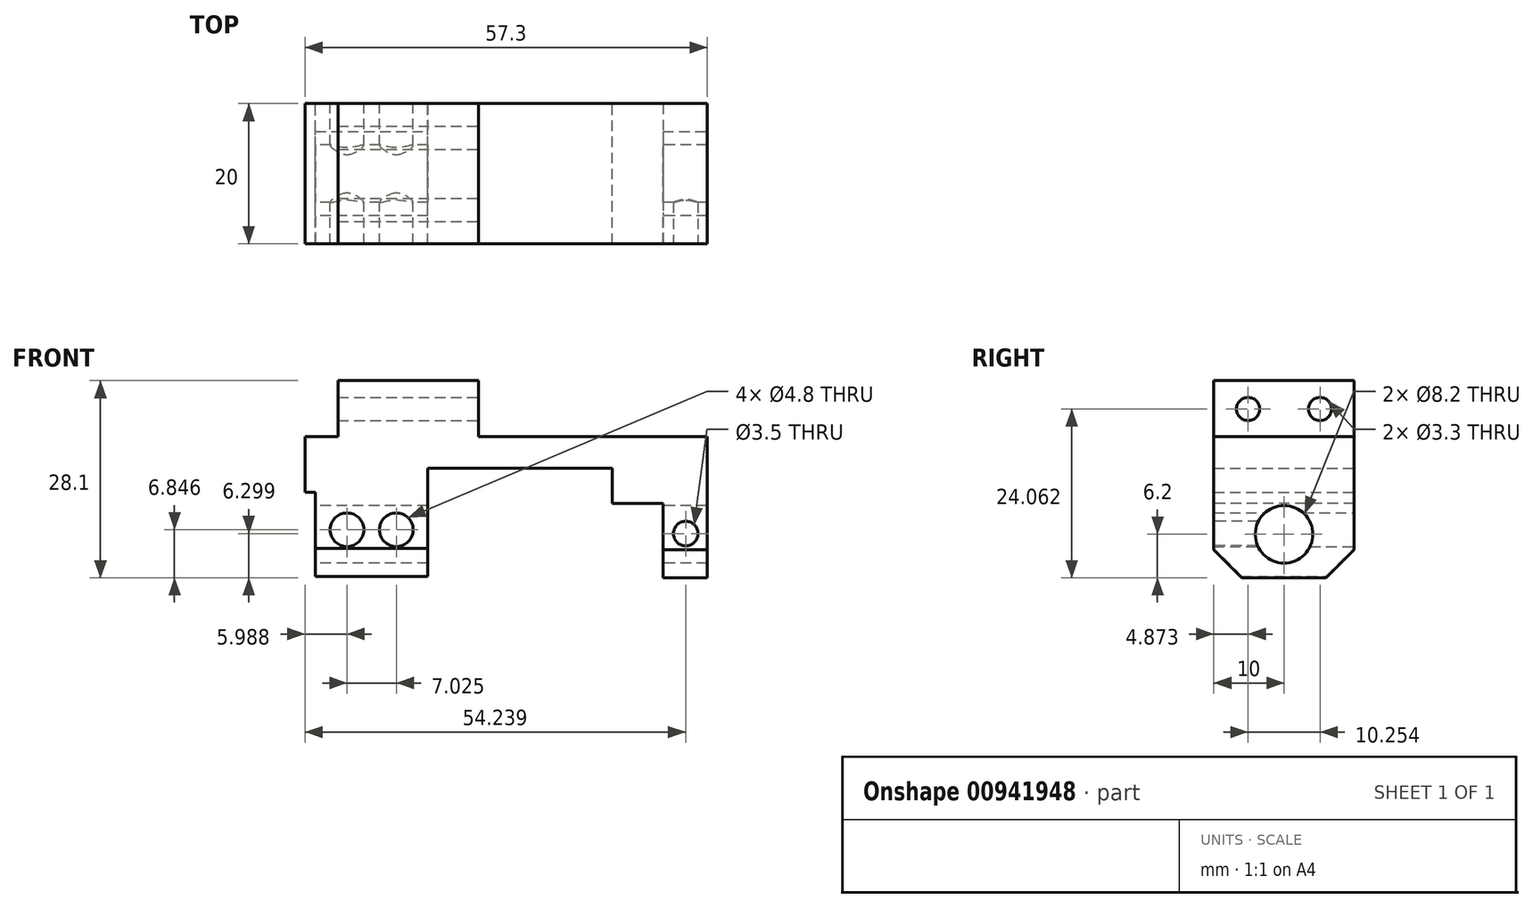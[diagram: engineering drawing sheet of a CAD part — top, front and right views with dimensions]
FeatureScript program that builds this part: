
annotation { "Feature Type Name" : "Feature", "Feature Type Description" : "" }
export const myFeature = defineFeature(function(context is Context, id is Id, definition is map)
    precondition{}
    {
        {
            var Q0;
            Q0=qCreatedBy(makeId("Front.planeOp"),FACE);
            var sketch = newSketch(context, id + "F0", { "sketchPlane" : qUnion([Q0])});
            skPoint(sketch, "E0.middle", {"position": v(0, 0) * mm});
            skLineSegment(sketch, "E1", {"start": v(-27, 4.5) * mm, "end": v(-22.3, 4.5) * mm});
            skLineSegment(sketch, "E2", {"start": v(-22.3, 4.5) * mm, "end": v(-22.3, 12.5) * mm});
            skPoint(sketch, "E3.orphan", {"position": v(-24.1, 12.5) * mm});
            skLineSegment(sketch, "E4", {"start": v(-2.3, 12.5) * mm, "end": v(-2.3, 4.5) * mm});
            skLineSegment(sketch, "E5", {"start": v(-2.3, 4.5) * mm, "end": v(27, 4.5) * mm});
            skPoint(sketch, "E6.orphan", {"position": v(27, 14) * mm});
            skLineSegment(sketch, "E7", {"start": v(-22.3, 12.5) * mm, "end": v(-2.3, 12.5) * mm});
            skLineSegment(sketch, "E8", {"start": v(-27, 4.5) * mm, "end": v(-27, -3.4) * mm});
            skLineSegment(sketch, "E9", {"start": v(-27, -3.4) * mm, "end": v(-25.5, -3.4) * mm});
            skLineSegment(sketch, "E10", {"start": v(-25.5, -3.4) * mm, "end": v(-25.5, -15.4) * mm});
            skPoint(sketch, "E11.orphan", {"position": v(-27, -14) * mm});
            skLineSegment(sketch, "E12", {"start": v(-25.5, -15.4) * mm, "end": v(-9.5, -15.4) * mm});
            skPoint(sketch, "E0.right.end.orphan", {"position": v(24.1, -12.5) * mm});
            skLineSegment(sketch, "E13", {"start": v(27, 4.5) * mm, "end": v(27, 0) * mm});
            skLineSegment(sketch, "E14", {"start": v(-9.5, -15.4) * mm, "end": v(-9.5, 0) * mm});
            skLineSegment(sketch, "E15", {"start": v(-9.5, 0) * mm, "end": v(16.8, 0) * mm});
            skLineSegment(sketch, "E16", {"start": v(27, 0) * mm, "end": v(27, -5) * mm});
            skLineSegment(sketch, "E17", {"start": v(27, -5) * mm, "end": v(16.8, -5) * mm});
            skLineSegment(sketch, "E18", {"start": v(16.8, -5) * mm, "end": v(16.8, 0) * mm});
            skSolve(sketch);
        }
        {
            var Q0;
            Q0 = qSketchRegion(id + "F0", true);
            extrude(context, id + "F1", {"entities" : qUnion([Q0]), "endBound" : BoundingType.SYMMETRIC, "depth" : 20 * mm, "offsetDistance" : 25 * mm});
        }
        {
            var Q0;
            Q0=makeQuery(id+"F1.opExtrude","CAP_EDGE",EDGE,{"disambiguationData":[OSD([sQuery(id+"F0.wireOp",EDGE,"E12")])],"isStart":false});
            var Q1;
            Q1=makeQuery(id+"F1.opExtrude","CAP_EDGE",EDGE,{"disambiguationData":[OSD([sQuery(id+"F0.wireOp",EDGE,"E12")])],"isStart":true});
            chamfer(context, id + "F2", {"entities" : qUnion([Q0, Q1]), "width" : 4 * mm, "tangentPropagation" : true});
        }
        {
            var Q0;
            Q0=makeQuery(id+"F1.opExtrude","SWEPT_FACE",FACE,{"disambiguationData":[OSD([sQuery(id+"F0.wireOp",EDGE,"E10")])]});
            var sketch = newSketch(context, id + "F3", { "sketchPlane" : qUnion([Q0])});
            skLineSegment(sketch, "E19", {"start": v(0, -3.4) * mm, "end": v(0, -15.4) * mm});
            skCircle(sketch, "E20", {"center": v(0, -9.4) * mm, "radius": 4.1 * mm});
            skSolve(sketch);
        }
        {
            var Q0;
            Q0=makeQuery(id+"F1.opExtrude","SWEPT_FACE",FACE,{"disambiguationData":[OSD([sQuery(id+"F0.wireOp",EDGE,"E13"),sQuery(id+"F0.wireOp",EDGE,"E16")])]});
            var sketch = newSketch(context, id + "F4", { "sketchPlane" : qUnion([Q0])});
            skLineSegment(sketch, "E21", {"start": v(10, 4.5) * mm, "end": v(10, -15.6) * mm});
            skLineSegment(sketch, "E22", {"start": v(10, -15.6) * mm, "end": v(-10, -15.6) * mm});
            skPoint(sketch, "E23.end.orphan", {"position": v(-10, -14.05) * mm});
            skLineSegment(sketch, "E24", {"start": v(-10, -15.6) * mm, "end": v(-10, 4.5) * mm});
            skLineSegment(sketch, "E25", {"start": v(-10, 4.5) * mm, "end": v(10, 4.5) * mm});
            skSolve(sketch);
        }
        {
            var Q0;
            Q0 = qSketchRegion(id + "F4", true);
            extrude(context, id + "F5", {"entities" : qUnion([Q0]), "operationType" : NewBodyOperationType.ADD, "depth" : 3.3 * mm, "offsetDistance" : 25 * mm, "hasSecondDirection" : true, "secondDirectionOppositeDirection" : true, "secondDirectionDepth" : 3 * mm});
        }
        {
            var Q0;
            {var subQ0=sQuery(id+"F3.wireOp",EDGE,"E20");var subQ1=sQuery(id+"F3.wireOp",EDGE,"E19");var subQ2=makeQuery(id+"F3.imprint","INTERSECT",VERTEX,{"disambiguationData":[OD(0.0)],"derivedFrom":[subQ1,subQ0]});Q0=makeQuery(id+"F3.imprint","IMPRINT",FACE,{"disambiguationData":[TD([[makeQuery(id+"F3.imprint","IMPRINT",EDGE,{"disambiguationData":[TD([[subQ2,-1.0]])],"derivedFrom":subQ1}),1.0]])]});}
            var Q1;
            {var subQ0=sQuery(id+"F3.wireOp",EDGE,"E20");var subQ1=sQuery(id+"F3.wireOp",EDGE,"E19");var subQ2=makeQuery(id+"F3.imprint","INTERSECT",VERTEX,{"disambiguationData":[OD(0.0)],"derivedFrom":[subQ1,subQ0]});Q1=makeQuery(id+"F3.imprint","IMPRINT",FACE,{"disambiguationData":[TD([[makeQuery(id+"F3.imprint","IMPRINT",EDGE,{"disambiguationData":[TD([[subQ2,-1.0]])],"derivedFrom":subQ1}),-1.0]])]});}
            extrude(context, id + "F6", {"entities" : qUnion([Q0, Q1]), "operationType" : NewBodyOperationType.REMOVE, "oppositeDirection" : true, "depth" : 84 * mm, "offsetDistance" : 25 * mm});
        }
        {
            var Q0;
            Q0=makeQuery(id+"F5.opExtrude","SWEPT_EDGE",EDGE,{"disambiguationData":[OSD([sQuery(id+"F4.wireOp",EDGE,"E21"),sQuery(id+"F4.wireOp",EDGE,"E22")])]});
            var Q1;
            Q1=makeQuery(id+"F5.opExtrude","SWEPT_EDGE",EDGE,{"disambiguationData":[OSD([sQuery(id+"F4.wireOp",EDGE,"E22"),sQuery(id+"F4.wireOp",EDGE,"E24")])]});
            chamfer(context, id + "F7", {"entities" : qUnion([Q0, Q1]), "width" : 4 * mm, "tangentPropagation" : true});
        }
        {
            var Q0;
            Q0=makeQuery(id+"F5.boolean.opBoolean","MERGE",FACE,{"derivedFrom":[makeQuery(id+"F1.opExtrude","CAP_FACE",FACE,{"disambiguationData":[OSD([sQuery(id+"F0.wireOp",EDGE,"E1"),sQuery(id+"F0.wireOp",EDGE,"E2"),sQuery(id+"F0.wireOp",EDGE,"E4"),sQuery(id+"F0.wireOp",EDGE,"E5"),sQuery(id+"F0.wireOp",EDGE,"E7"),sQuery(id+"F0.wireOp",EDGE,"E8"),sQuery(id+"F0.wireOp",EDGE,"E9"),sQuery(id+"F0.wireOp",EDGE,"E10"),sQuery(id+"F0.wireOp",EDGE,"E12"),sQuery(id+"F0.wireOp",EDGE,"E13"),sQuery(id+"F0.wireOp",EDGE,"E14"),sQuery(id+"F0.wireOp",EDGE,"E15"),sQuery(id+"F0.wireOp",EDGE,"E16"),sQuery(id+"F0.wireOp",EDGE,"E17"),sQuery(id+"F0.wireOp",EDGE,"E18")])],"isStart":false}),makeQuery(id+"F5.opExtrude","SWEPT_FACE",FACE,{"disambiguationData":[OSD([sQuery(id+"F4.wireOp",EDGE,"E24")])]})]});
            var sketch = newSketch(context, id + "F8", { "sketchPlane" : qUnion([Q0])});
            skCircle(sketch, "E26", {"center": v(27.24, -9.3) * mm, "radius": 1.75 * mm});
            skSolve(sketch);
        }
        {
            var Q0;
            Q0 = qSketchRegion(id + "F8", true);
            extrude(context, id + "F9", {"entities" : qUnion([Q0]), "operationType" : NewBodyOperationType.REMOVE, "oppositeDirection" : true, "depth" : 8.7 * mm, "offsetDistance" : 25 * mm});
        }
        {
            var Q0;
            Q0=makeQuery(id+"F5.opExtrude","CAP_FACE",FACE,{"disambiguationData":[OSD([sQuery(id+"F4.wireOp",EDGE,"E21"),sQuery(id+"F4.wireOp",EDGE,"E22"),sQuery(id+"F4.wireOp",EDGE,"E24"),sQuery(id+"F4.wireOp",EDGE,"E25")])],"isStart":false});
            var sketch = newSketch(context, id + "F10", { "sketchPlane" : qUnion([Q0])});
            skLineSegment(sketch, "E27", {"start": v(10, 4.5) * mm, "end": v(10, 12.42) * mm});
            skLineSegment(sketch, "E28", {"start": v(10, 8.46) * mm, "end": v(6.75, 8.46) * mm});
            skCircle(sketch, "E29", {"center": v(5.13, 8.46) * mm, "radius": 1.65 * mm});
            skLineSegment(sketch, "E30", {"start": v(0, 0) * mm, "end": v(0, 3.04) * mm});
            skCircle(sketch, "E31.MirrorC", {"center": v(-5.13, 8.46) * mm, "radius": 1.65 * mm});
            skSolve(sketch);
        }
        {
            var Q0;
            Q0 = qSketchRegion(id + "F10", true);
            extrude(context, id + "F11", {"entities" : qUnion([Q0]), "operationType" : NewBodyOperationType.REMOVE, "oppositeDirection" : true, "depth" : 66.9 * mm, "offsetDistance" : 25 * mm});
        }
        {
            var Q0;
            Q0=makeQuery(id+"F5.boolean.opBoolean","MERGE",FACE,{"derivedFrom":[makeQuery(id+"F1.opExtrude","CAP_FACE",FACE,{"disambiguationData":[OSD([sQuery(id+"F0.wireOp",EDGE,"E1"),sQuery(id+"F0.wireOp",EDGE,"E2"),sQuery(id+"F0.wireOp",EDGE,"E4"),sQuery(id+"F0.wireOp",EDGE,"E5"),sQuery(id+"F0.wireOp",EDGE,"E7"),sQuery(id+"F0.wireOp",EDGE,"E8"),sQuery(id+"F0.wireOp",EDGE,"E9"),sQuery(id+"F0.wireOp",EDGE,"E10"),sQuery(id+"F0.wireOp",EDGE,"E12"),sQuery(id+"F0.wireOp",EDGE,"E13"),sQuery(id+"F0.wireOp",EDGE,"E14"),sQuery(id+"F0.wireOp",EDGE,"E15"),sQuery(id+"F0.wireOp",EDGE,"E16"),sQuery(id+"F0.wireOp",EDGE,"E17"),sQuery(id+"F0.wireOp",EDGE,"E18")])],"isStart":true}),makeQuery(id+"F5.opExtrude","SWEPT_FACE",FACE,{"disambiguationData":[OSD([sQuery(id+"F4.wireOp",EDGE,"E21")])]})]});
            var sketch = newSketch(context, id + "F12", { "sketchPlane" : qUnion([Q0])});
            skCircle(sketch, "E32", {"center": v(21.01, -8.75) * mm, "radius": 2.4 * mm});
            skLineSegment(sketch, "E33", {"start": v(9.5, -11.4) * mm, "end": v(25.5, -11.4) * mm});
            skLineSegment(sketch, "E34", {"start": v(17.5, -11.4) * mm, "end": v(17.5, -14.88) * mm});
            skCircle(sketch, "E35.MirrorC", {"center": v(13.99, -8.75) * mm, "radius": 2.4 * mm});
            skSolve(sketch);
        }
        {
            var Q0;
            Q0 = qSketchRegion(id + "F12", true);
            extrude(context, id + "F13", {"entities" : qUnion([Q0]), "operationType" : NewBodyOperationType.REMOVE, "oppositeDirection" : true, "depth" : 25 * mm, "offsetDistance" : 25 * mm});
        }
    });
